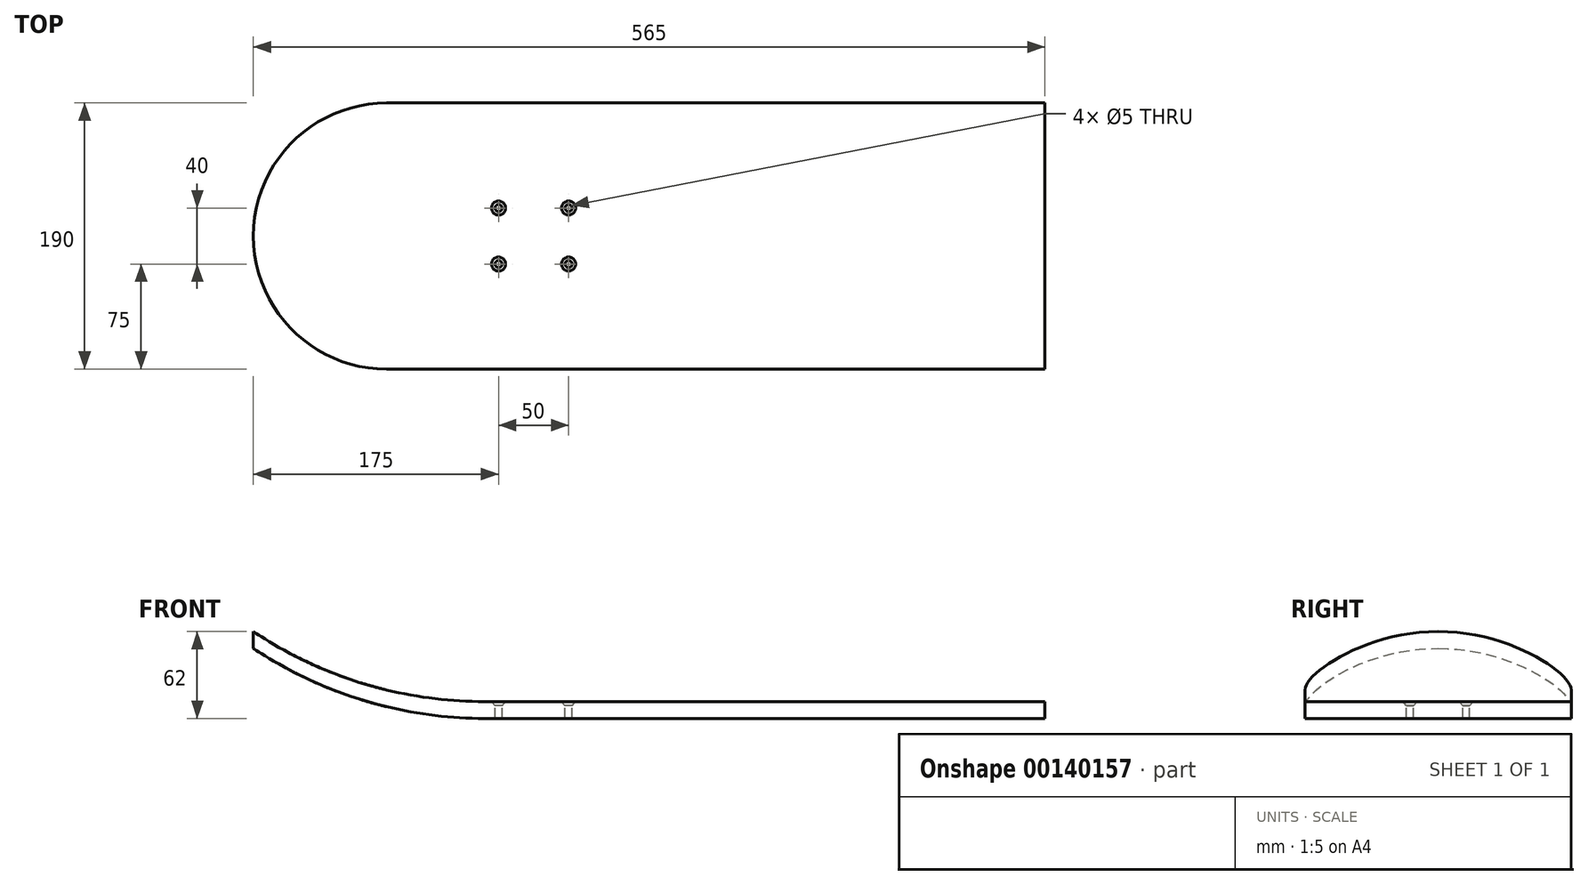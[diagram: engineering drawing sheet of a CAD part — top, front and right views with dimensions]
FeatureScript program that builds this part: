
annotation { "Feature Type Name" : "Feature", "Feature Type Description" : "" }
export const myFeature = defineFeature(function(context is Context, id is Id, definition is map)
    precondition{}
    {
        {
            var Q0;
            Q0=qCreatedBy(makeId("Right.planeOp"),FACE);
            var sketch = newSketch(context, id + "F0", { "sketchPlane" : qUnion([Q0])});
            skLineSegment(sketch, "E0.bottom", {"start": v(95, 6) * mm, "end": v(-95, 6) * mm});
            skLineSegment(sketch, "E0.top", {"start": v(95, -6) * mm, "end": v(-95, -6) * mm});
            skLineSegment(sketch, "E0.left", {"start": v(95, 6) * mm, "end": v(95, -6) * mm});
            skLineSegment(sketch, "E0.right", {"start": v(-95, 6) * mm, "end": v(-95, -6) * mm});
            skPoint(sketch, "E0.middle", {"position": v(0, 0) * mm});
            skSolve(sketch);
        }
        {
            var Q0;
            Q0 = qSketchRegion(id + "F0", true);
            extrude(context, id + "F1", {"entities" : qUnion([Q0]), "endBound" : BoundingType.SYMMETRIC, "offsetDistance" : 25 * mm, "depth" : 400 * mm});
        }
        {
            var Q0;
            Q0=makeQuery(id+"F1.opExtrude","SWEPT_FACE",FACE,{"disambiguationData":[OSD([sQuery(id+"F0.wireOp",EDGE,"E0.right")])]});
            var sketch = newSketch(context, id + "F2", { "sketchPlane" : qUnion([Q0])});
            skSolve(sketch);
        }
        {
            var Q0;
            {var subQ0=sQuery(id+"F0.wireOp",EDGE,"E0.right");Q0=makeQuery(id+"F2.imprint","IMPRINT",FACE,{"disambiguationData":[TD([[makeQuery(id+"F2.imprint","IMPRINT",EDGE,{"derivedFrom":makeQuery(id+"F1.opExtrude","CAP_EDGE",EDGE,{"disambiguationData":[OSD([subQ0])],"isStart":true})}),1.0]])]});}
            var sketch = newSketch(context, id + "F3", { "sketchPlane" : qUnion([Q0])});
            skArc(sketch, "E1", {"start": v(-365, 44) * mm, "mid": v(-286.2, 6.77) * mm, "end": v(-200, -6) * mm});
            skLineSegment(sketch, "E2", {"start": v(0, -6) * mm, "end": v(-200, -6) * mm, "construction": true});
            skLineSegment(sketch, "E3", {"start": v(-365, 44) * mm, "end": v(-365, 56) * mm});
            skLineSegment(sketch, "E4", {"start": v(-200, -6) * mm, "end": v(-200, 6) * mm});
            skArc(sketch, "E5", {"start": v(-365, 56) * mm, "mid": v(-286.2, 18.77) * mm, "end": v(-200, 6) * mm});
            skLineSegment(sketch, "E6", {"start": v(0, -6) * mm, "end": v(0, 6) * mm, "construction": true});
            skLineSegment(sketch, "E7", {"start": v(0, 6) * mm, "end": v(-200, 6) * mm, "construction": true});
            skSolve(sketch);
        }
        {
            var Q0;
            Q0 = qSketchRegion(id + "F3", true);
            extrude(context, id + "F4", {"entities" : qUnion([Q0]), "operationType" : NewBodyOperationType.ADD, "oppositeDirection" : true, "offsetDistance" : 25 * mm, "depth" : 190 * mm});
        }
        {
            var Q0;
            Q0=makeQuery(id+"F4.opExtrude","CAP_EDGE",EDGE,{"disambiguationData":[OSD([sQuery(id+"F3.wireOp",EDGE,"E3")])],"isStart":true});
            var Q1;
            Q1=makeQuery(id+"F4.opExtrude","CAP_EDGE",EDGE,{"disambiguationData":[OSD([sQuery(id+"F3.wireOp",EDGE,"E3")])],"isStart":false});
            fillet(context, id + "F5", {"entities" : qUnion([Q0, Q1]), "radius" : 95 * mm, "tangentPropagation" : true, "defaultsChanged" : false, "vertexSettings" : [], "allowEdgeOverflow" : false});
        }
        {
            var Q0;
            Q0=makeQuery(id+"F1.opExtrude","SWEPT_FACE",FACE,{"disambiguationData":[OSD([sQuery(id+"F0.wireOp",EDGE,"E0.bottom")])]});
            var sketch = newSketch(context, id + "F6", { "sketchPlane" : qUnion([Q0])});
            skLineSegment(sketch, "E8", {"start": v(0, 0) * mm, "end": v(-190, 0) * mm, "construction": true});
            skPoint(sketch, "E8.endSnap0", {"position": v(-200, 0) * mm});
            skLineSegment(sketch, "E9", {"start": v(-190, 0) * mm, "end": v(-190, 20) * mm, "construction": true});
            skLineSegment(sketch, "E10", {"start": v(-190, 20) * mm, "end": v(-140, 20) * mm, "construction": true});
            skLineSegment(sketch, "E11", {"start": v(-190, 0) * mm, "end": v(-190, -20) * mm, "construction": true});
            skLineSegment(sketch, "E12", {"start": v(-190, -20) * mm, "end": v(-140, -20) * mm, "construction": true});
            skSolve(sketch);
        }
        {
            var Q0;
            Q0=sQuery(id+"F6.wireOp",VERTEX,"E10.start");
            var Q1;
            Q1=sQuery(id+"F6.wireOp",VERTEX,"E10.end");
            var Q2;
            Q2=sQuery(id+"F6.wireOp",VERTEX,"E12.end");
            var Q3;
            Q3=sQuery(id+"F6.wireOp",VERTEX,"E12.start");
            var Q4;
            Q4=makeQuery(id+"F1.opExtrude","SWEPT_BODY",BODY,{"disambiguationData":[OSD([sQuery(id+"F0.wireOp",EDGE,"E0.bottom"),sQuery(id+"F0.wireOp",EDGE,"E0.top"),sQuery(id+"F0.wireOp",EDGE,"E0.left"),sQuery(id+"F0.wireOp",EDGE,"E0.right")])]});
            hole(context, id + "F7", {"style" : HoleStyle.C_SINK, "endStyle" : HoleEndStyle.THROUGH, "holeDiameter" : 5 * mm, "cSinkDiameter" : 10 * mm, "cSinkAngle" : 82 * degree, "locations" : qUnion([Q0, Q1, Q2, Q3]), "scope" : qUnion([Q4]), "isTappedThrough" : true});
        }
    });
